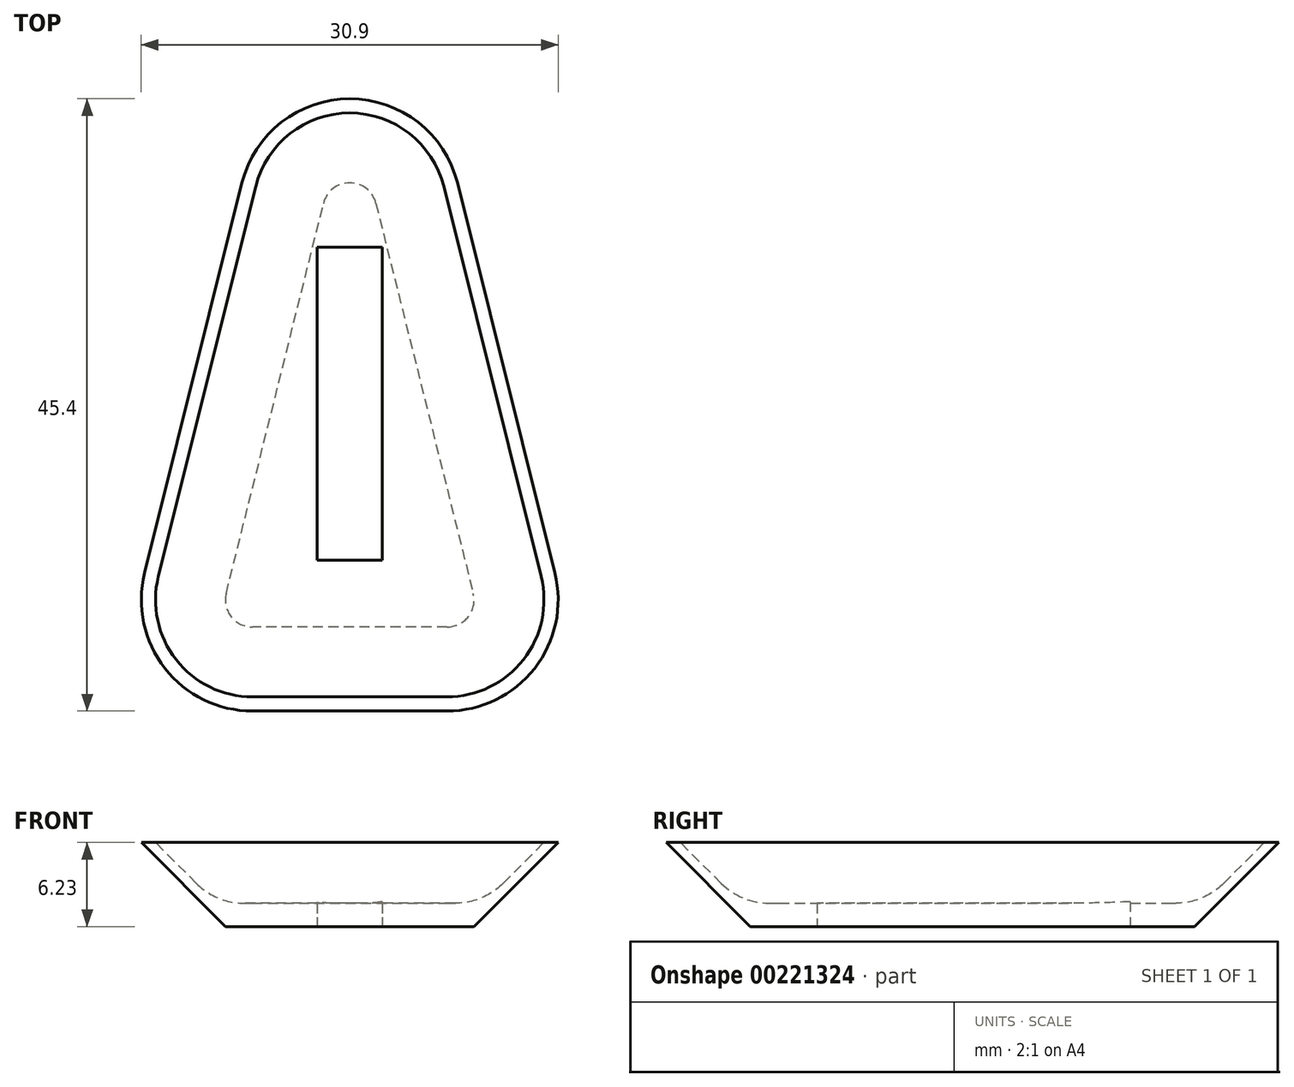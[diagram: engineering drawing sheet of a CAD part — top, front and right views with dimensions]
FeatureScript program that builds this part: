
annotation { "Feature Type Name" : "Feature", "Feature Type Description" : "" }
export const myFeature = defineFeature(function(context is Context, id is Id, definition is map)
    precondition{}
    {
        {
            var Q0;
            Q0=qCreatedBy(makeId("Top.planeOp"),FACE);
            var sketch = newSketch(context, id + "F0", { "sketchPlane" : qUnion([Q0])});
            skLineSegment(sketch, "E0", {"start": v(0, 0) * mm, "end": v(-49.87, -200) * mm, "construction": true});
            skLineSegment(sketch, "E1", {"start": v(-49.87, -200) * mm, "end": v(49.87, -200) * mm, "construction": true});
            skLineSegment(sketch, "E2", {"start": v(49.87, -200) * mm, "end": v(0, 0) * mm, "construction": true});
            skLineSegment(sketch, "E3", {"start": v(0, 0) * mm, "end": v(0, -200) * mm, "construction": true});
            skLineSegment(sketch, "E4", {"start": v(-38.15, -153) * mm, "end": v(38.15, -153) * mm, "construction": true});
            skLineSegment(sketch, "E5.bottom", {"start": v(2.25, -164.5) * mm, "end": v(-2.25, -164.5) * mm, "construction": true});
            skLineSegment(sketch, "E5.top", {"start": v(2.25, -141.5) * mm, "end": v(-2.25, -141.5) * mm, "construction": true});
            skLineSegment(sketch, "E5.left", {"start": v(2.25, -164.5) * mm, "end": v(2.25, -141.5) * mm, "construction": true});
            skLineSegment(sketch, "E5.right", {"start": v(-2.25, -164.5) * mm, "end": v(-2.25, -141.5) * mm, "construction": true});
            skPoint(sketch, "E5.middle", {"position": v(0, -153) * mm});
            skLineSegment(sketch, "E6", {"start": v(-29.67, -119) * mm, "end": v(29.67, -119) * mm, "construction": true});
            skLineSegment(sketch, "E7", {"start": v(-46.62, -187) * mm, "end": v(46.62, -187) * mm, "construction": true});
            skLineSegment(sketch, "E8.bottom", {"start": v(2.25, -106.6) * mm, "end": v(-2.25, -106.6) * mm, "construction": true});
            skLineSegment(sketch, "E8.top", {"start": v(2.25, -83.6) * mm, "end": v(-2.25, -83.6) * mm, "construction": true});
            skLineSegment(sketch, "E8.left", {"start": v(2.25, -106.6) * mm, "end": v(2.25, -83.6) * mm, "construction": true});
            skLineSegment(sketch, "E8.right", {"start": v(-2.25, -106.6) * mm, "end": v(-2.25, -83.6) * mm, "construction": true});
            skPoint(sketch, "E8.middle", {"position": v(0, -95.1) * mm});
            skLineSegment(sketch, "E9.1.0.0", {"start": v(120, 0) * mm, "end": v(70.13, -200) * mm, "construction": true});
            skLineSegment(sketch, "E9.1.0.1", {"start": v(120, 0) * mm, "end": v(120, -200) * mm, "construction": true});
            skLineSegment(sketch, "E9.1.0.2", {"start": v(169.87, -200) * mm, "end": v(120, 0) * mm, "construction": true});
            skLineSegment(sketch, "E9.direction1", {"start": v(-49.87, -200) * mm, "end": v(70.13, -200) * mm, "construction": true});
            skLineSegment(sketch, "E10.bottom", {"start": v(117.75, -83.6) * mm, "end": v(122.25, -83.6) * mm, "construction": true});
            skLineSegment(sketch, "E10.top", {"start": v(117.75, -106.6) * mm, "end": v(122.25, -106.6) * mm, "construction": true});
            skLineSegment(sketch, "E10.left", {"start": v(117.75, -83.6) * mm, "end": v(117.75, -106.6) * mm, "construction": true});
            skLineSegment(sketch, "E10.right", {"start": v(122.25, -83.6) * mm, "end": v(122.25, -106.6) * mm, "construction": true});
            skPoint(sketch, "E10.middle", {"position": v(120, -95.1) * mm});
            skLineSegment(sketch, "E11", {"start": v(101.52, -74.1) * mm, "end": v(138.48, -74.1) * mm, "construction": true});
            skLineSegment(sketch, "E12", {"start": v(91.05, -116.1) * mm, "end": v(148.95, -116.1) * mm, "construction": true});
            skLineSegment(sketch, "E13.bottom", {"start": v(2.25, -59.9) * mm, "end": v(-2.25, -59.9) * mm, "construction": true});
            skLineSegment(sketch, "E13.top", {"start": v(2.25, -36.9) * mm, "end": v(-2.25, -36.9) * mm, "construction": true});
            skLineSegment(sketch, "E13.left", {"start": v(2.25, -59.9) * mm, "end": v(2.25, -36.9) * mm, "construction": true});
            skLineSegment(sketch, "E13.right", {"start": v(-2.25, -59.9) * mm, "end": v(-2.25, -36.9) * mm, "construction": true});
            skPoint(sketch, "E13.middle", {"position": v(0, -48.4) * mm});
            skLineSegment(sketch, "E14", {"start": v(-17.75, -71.2) * mm, "end": v(17.75, -71.2) * mm, "construction": true});
            skLineSegment(sketch, "E15", {"start": v(-9.15, -62.48) * mm, "end": v(-1.94, -33.55) * mm});
            skArc(sketch, "E16", {"start": v(1.94, -33.55) * mm, "mid": v(0, -32.03) * mm, "end": v(-1.94, -33.55) * mm});
            skLineSegment(sketch, "E17.MirrorCS", {"start": v(9.15, -62.48) * mm, "end": v(1.94, -33.55) * mm});
            skLineSegment(sketch, "E18", {"start": v(-7.21, -64.97) * mm, "end": v(7.21, -64.97) * mm});
            skPoint(sketch, "E19.visualSharp", {"position": v(-9.77, -64.97) * mm});
            skArc(sketch, "E19.filletArc", {"start": v(-9.15, -62.48) * mm, "mid": v(-8.79, -64.2) * mm, "end": v(-7.21, -64.97) * mm});
            skPoint(sketch, "E20.visualSharp", {"position": v(9.77, -64.97) * mm});
            skArc(sketch, "E20.filletArc", {"start": v(7.21, -64.97) * mm, "mid": v(8.79, -64.2) * mm, "end": v(9.15, -62.48) * mm});
            skSolve(sketch);
        }
        {
            var Q0;
            Q0 = qSketchRegion(id + "F0", true);
            extrude(context, id + "F1", {"entities" : qUnion([Q0]), "depth" : 6.23 * mm, "hasDraft" : true, "draftAngle" : 45 * degree});
        }
        {
            var Q0;
            Q0=makeQuery(id+"F1.opExtrude","CAP_FACE",FACE,{"disambiguationData":[OSD([sQuery(id+"F0.wireOp",EDGE,"E15"),sQuery(id+"F0.wireOp",EDGE,"E16"),sQuery(id+"F0.wireOp",EDGE,"E17.MirrorCS"),sQuery(id+"F0.wireOp",EDGE,"E18"),sQuery(id+"F0.wireOp",EDGE,"E19.filletArc"),sQuery(id+"F0.wireOp",EDGE,"E20.filletArc")])],"isStart":false});
            var sketch = newSketch(context, id + "F2", { "sketchPlane" : qUnion([Q0])});
            skArc(sketch, "E21.0", {"start": v(7.99, -32.04) * mm, "mid": v(0, -25.8) * mm, "end": v(-7.99, -32.04) * mm, "construction": true});
            skArc(sketch, "E21.1", {"start": v(-15.2, -60.97) * mm, "mid": v(-13.7, -68.04) * mm, "end": v(-7.21, -71.2) * mm, "construction": true});
            skArc(sketch, "E21.2", {"start": v(7.21, -71.2) * mm, "mid": v(13.7, -68.04) * mm, "end": v(15.2, -60.97) * mm, "construction": true});
            skLineSegment(sketch, "E22", {"start": v(-7.99, -32.04) * mm, "end": v(-15.2, -60.97) * mm, "construction": true});
            skLineSegment(sketch, "E23", {"start": v(7.99, -32.04) * mm, "end": v(15.2, -60.97) * mm, "construction": true});
            skLineSegment(sketch, "E24", {"start": v(-7.21, -71.2) * mm, "end": v(7.21, -71.2) * mm, "construction": true});
            skLineSegment(sketch, "E25.0", {"start": v(6.97, -32.3) * mm, "end": v(14.18, -61.23) * mm});
            skLineSegment(sketch, "E25.1", {"start": v(-6.97, -32.3) * mm, "end": v(-14.18, -61.23) * mm});
            skArc(sketch, "E25.2", {"start": v(-14.18, -61.23) * mm, "mid": v(-12.87, -67.39) * mm, "end": v(-7.21, -70.15) * mm});
            skArc(sketch, "E25.3", {"start": v(6.97, -32.3) * mm, "mid": v(0, -26.85) * mm, "end": v(-6.97, -32.3) * mm});
            skLineSegment(sketch, "E25.4", {"start": v(-7.21, -70.15) * mm, "end": v(7.21, -70.15) * mm});
            skArc(sketch, "E25.5", {"start": v(7.21, -70.15) * mm, "mid": v(12.87, -67.39) * mm, "end": v(14.18, -61.23) * mm});
            skSolve(sketch);
        }
        {
            var Q0;
            Q0 = qSketchRegion(id + "F2", true);
            extrude(context, id + "F3", {"entities" : qUnion([Q0]), "operationType" : NewBodyOperationType.REMOVE, "oppositeDirection" : true, "depth" : 4.5 * mm, "hasDraft" : true, "draftAngle" : 45 * degree, "draftPullDirection" : true});
        }
        {
            var Q0;
            Q0=makeQuery(id+"F0.imprint","IMPRINT",FACE,{"disambiguationData":[TD([[makeQuery(id+"F0.imprint","IMPRINT",EDGE,{"derivedFrom":sQuery(id+"F0.wireOp",EDGE,"E15")}),-1.0]])]});
            var sketch = newSketch(context, id + "F4", { "sketchPlane" : qUnion([Q0])});
            skLineSegment(sketch, "E26.bottom", {"start": v(-2.4, -60) * mm, "end": v(2.4, -60) * mm});
            skLineSegment(sketch, "E26.top", {"start": v(-2.4, -36.8) * mm, "end": v(2.4, -36.8) * mm});
            skLineSegment(sketch, "E26.left", {"start": v(-2.4, -60) * mm, "end": v(-2.4, -36.8) * mm});
            skLineSegment(sketch, "E26.right", {"start": v(2.4, -60) * mm, "end": v(2.4, -36.8) * mm});
            skPoint(sketch, "E26.middle", {"position": v(0, -48.4) * mm});
            skSolve(sketch);
        }
        {
            var Q0;
            Q0 = qSketchRegion(id + "F4", true);
            extrude(context, id + "F5", {"entities" : qUnion([Q0]), "operationType" : NewBodyOperationType.REMOVE, "endBound" : BoundingType.THROUGH_ALL, "depth" : 25 * mm});
        }
        {
            var Q0;
            Q0=makeQuery(id+"F3.boolean.opBoolean","COPY",EDGE,{"derivedFrom":makeQuery(id+"F3.opExtrude","CAP_EDGE",EDGE,{"disambiguationData":[OSD([sQuery(id+"F2.wireOp",EDGE,"E25.1")])],"isStart":false})});
            fillet(context, id + "F6", {"entities" : qUnion([Q0]), "radius" : 5 * mm, "tangentPropagation" : true, "allowEdgeOverflow" : false});
        }
    });
